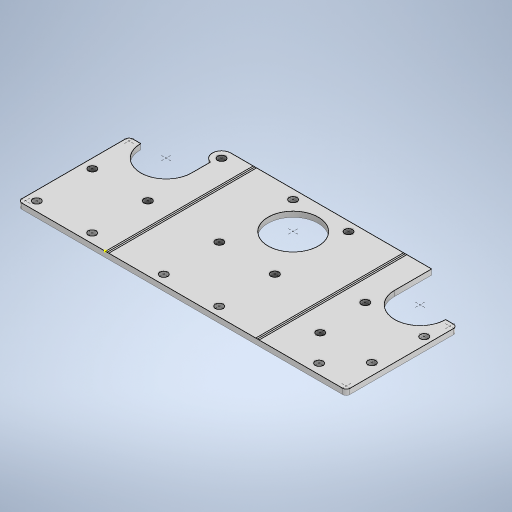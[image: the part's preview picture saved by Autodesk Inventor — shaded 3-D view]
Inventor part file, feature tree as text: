
AUTODESK INVENTOR PART (.ipt)
format: ipt  version: 2024.2 (Build 282272000, 272)  size: 273,920 bytes
history: native  units: in
note: dims shown in document units (in); Inventor stores cm internally (conversion verified against a paired STEP export)
features: sketch x1, extrude x1
ambient origin geometry x8: Origin, YZ Plane, XZ Plane, XY Plane, X Axis, Y Axis, Z Axis, Center Point
bodies: Solid1 (feature_tree)
feature tree (2):
  sketch  "Sketch1"  dims[d0=0.0591in d1=0.0in]
  extrude  "Extrusion1"  [1 undecoded]
note: 1 required parameter value undecoded (feature->parameter linkage not recoverable at this tier; creation-order binding heuristic only, values carry confidence <= 0.55)
